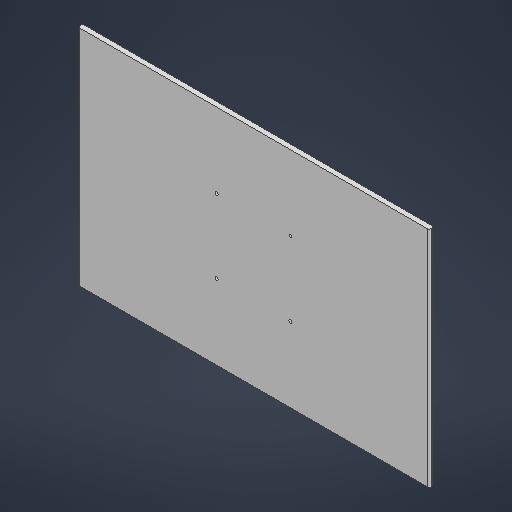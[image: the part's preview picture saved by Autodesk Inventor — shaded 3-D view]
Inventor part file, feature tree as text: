
AUTODESK INVENTOR PART (.ipt)
format: ipt  version: 2025.1 (Build 291241000, 241)  size: 196,096 bytes
history: native  units: mm
features: sketch x3, extrude x2, hole x1, fillet x1
ambient origin geometry x8: Origin, YZ Plane, XZ Plane, XY Plane, X Axis, Y Axis, Z Axis, Center Point
bodies: Solid1 (feature_tree)
feature tree (7):
  extrude  "Extrusion1"  Depth=227.0mm
  hole  "Hole1"  [1 undecoded]
  fillet  "Fillet1"  Radius=75.0mm
  extrude  "Extrusion2"  Depth=2.0mm
  sketch  "Sketch1"  dims[d0=357.0mm d1=227.0mm]
  sketch  "Sketch2"  dims[d2=5.0mm d3=0.0mm d4=75.0mm d5=75.0mm]
  sketch  "Sketch3"  dims[d6=3.0mm d7=6.0mm d8=10.0mm d9=4.0mm d10=90.0deg d11=3.0mm d12=0.0mm d13=2.0mm d14=1.0mm d15=0.0mm]
note: 1 required parameter value undecoded (feature->parameter linkage not recoverable at this tier; creation-order binding heuristic only, values carry confidence <= 0.55)
